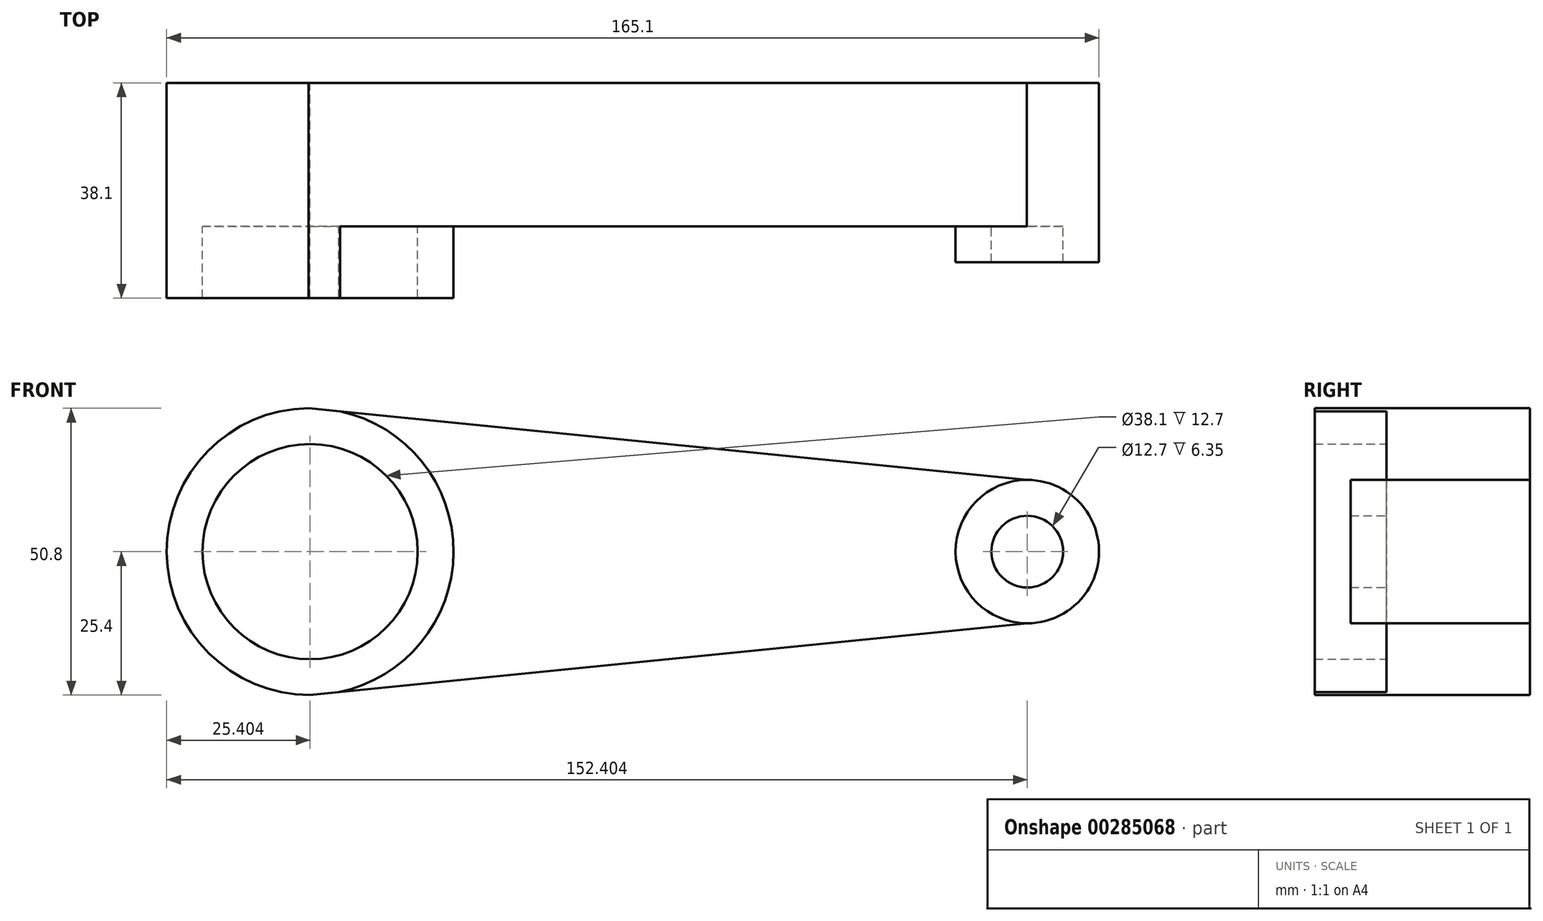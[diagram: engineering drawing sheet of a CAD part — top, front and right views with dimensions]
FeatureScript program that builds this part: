
annotation { "Feature Type Name" : "Feature", "Feature Type Description" : "" }
export const myFeature = defineFeature(function(context is Context, id is Id, definition is map)
    precondition{}
    {
        {
            var Q0;
            Q0=qCreatedBy(makeId("Front.planeOp"),FACE);
            var sketch = newSketch(context, id + "F0", { "sketchPlane" : qUnion([Q0])});
            skCircle(sketch, "E0", {"center": v(-62.17, 0) * mm, "radius": 25.4 * mm});
            skCircle(sketch, "E1", {"center": v(-62.17, 0) * mm, "radius": 19.05 * mm});
            skCircle(sketch, "E2", {"center": v(64.83, 0) * mm, "radius": 6.35 * mm});
            skCircle(sketch, "E3", {"center": v(64.83, 0) * mm, "radius": 12.7 * mm});
            skLineSegment(sketch, "E4", {"start": v(64.73, 12.7) * mm, "end": v(-62.46, 25.4) * mm});
            skLineSegment(sketch, "E5", {"start": v(64.87, -12.7) * mm, "end": v(-62.18, -25.4) * mm});
            skArc(sketch, "E6", {"start": v(26.73, -6.35) * mm, "mid": v(33.08, 0) * mm, "end": v(26.73, 6.35) * mm});
            skArc(sketch, "E7", {"start": v(-24.07, 6.35) * mm, "mid": v(-30.42, 0) * mm, "end": v(-24.07, -6.35) * mm});
            skLineSegment(sketch, "E8", {"start": v(-24.07, 6.35) * mm, "end": v(26.73, 6.35) * mm});
            skLineSegment(sketch, "E9", {"start": v(-24.07, -6.35) * mm, "end": v(26.73, -6.35) * mm});
            skLineSegment(sketch, "E10", {"start": v(26.73, -6.35) * mm, "end": v(-24.07, -6.35) * mm});
            skSolve(sketch);
        }
        {
            var Q0;
            Q0=makeQuery(id+"F0.imprint","IMPRINT",FACE,{"disambiguationData":[TD([[makeQuery(id+"F0.imprint","IMPRINT",EDGE,{"derivedFrom":sQuery(id+"F0.wireOp",EDGE,"E1")}),-1.0]])]});
            extrude(context, id + "F1", {"entities" : qUnion([Q0]), "depth" : 38.1 * mm});
        }
        {
            var Q0;
            Q0=makeQuery(id+"F0.imprint","IMPRINT",FACE,{"disambiguationData":[TD([[makeQuery(id+"F0.imprint","IMPRINT",EDGE,{"derivedFrom":sQuery(id+"F0.wireOp",EDGE,"E2")}),-1.0]])]});
            extrude(context, id + "F2", {"entities" : qUnion([Q0]), "operationType" : NewBodyOperationType.ADD, "depth" : 31.75 * mm});
        }
        {
            var Q0;
            Q0=makeQuery(id+"F0.imprint","IMPRINT",FACE,{"disambiguationData":[TD([[makeQuery(id+"F0.imprint","IMPRINT",EDGE,{"derivedFrom":sQuery(id+"F0.wireOp",EDGE,"E6")}),-1.0]])]});
            var Q1;
            Q1=makeQuery(id+"F0.imprint","IMPRINT",FACE,{"disambiguationData":[TD([[makeQuery(id+"F0.imprint","IMPRINT",EDGE,{"derivedFrom":sQuery(id+"F0.wireOp",EDGE,"E2")}),1.0]])]});
            var Q2;
            Q2=makeQuery(id+"F0.imprint","IMPRINT",FACE,{"disambiguationData":[TD([[makeQuery(id+"F0.imprint","IMPRINT",EDGE,{"derivedFrom":sQuery(id+"F0.wireOp",EDGE,"E1")}),1.0]])]});
            var Q3;
            Q3=makeQuery(id+"F0.imprint","IMPRINT",FACE,{"disambiguationData":[TD([[makeQuery(id+"F0.imprint","IMPRINT",EDGE,{"derivedFrom":sQuery(id+"F0.wireOp",EDGE,"E6")}),1.0]])]});
            extrude(context, id + "F3", {"entities" : qUnion([Q0, Q1, Q2, Q3]), "operationType" : NewBodyOperationType.ADD, "depth" : 25.4 * mm});
        }
        {
            var Q0;
            Q0=makeQuery(id+"F0.imprint","IMPRINT",FACE,{"disambiguationData":[TD([[makeQuery(id+"F0.imprint","IMPRINT",EDGE,{"derivedFrom":sQuery(id+"F0.wireOp",EDGE,"E2")}),-1.0]])]});
            extrude(context, id + "F4", {"entities" : qUnion([Q0]), "operationType" : NewBodyOperationType.ADD, "depth" : 31.75 * mm});
        }
    });
